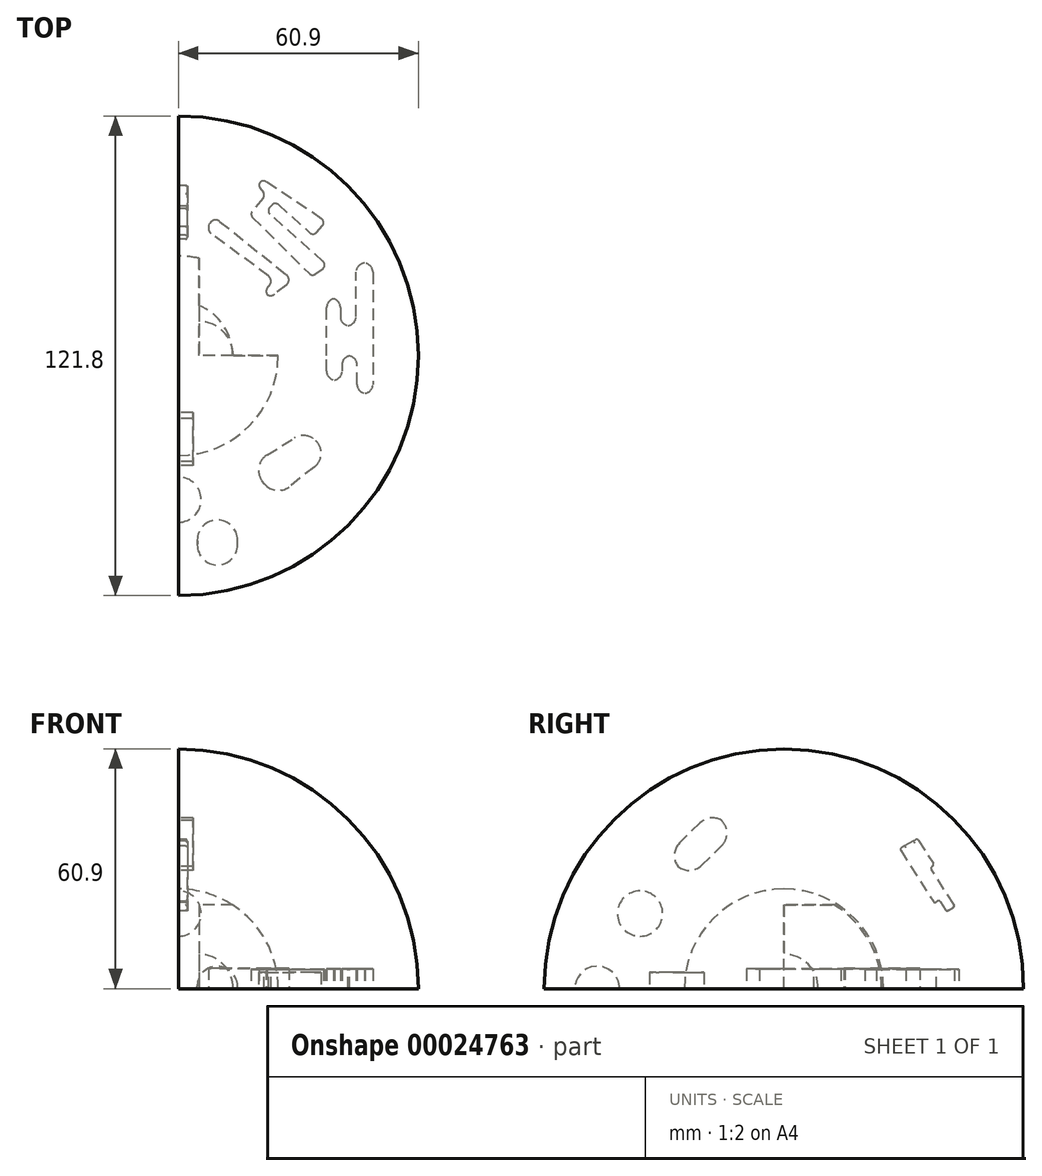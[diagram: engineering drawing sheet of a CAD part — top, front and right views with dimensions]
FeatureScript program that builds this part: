
annotation { "Feature Type Name" : "Feature", "Feature Type Description" : "" }
export const myFeature = defineFeature(function(context is Context, id is Id, definition is map)
    precondition{}
    {
        {
            var Q0;
            Q0=qCreatedBy(makeId("Front.planeOp"),FACE);
            var sketch = newSketch(context, id + "F0", { "sketchPlane" : qUnion([Q0])});
            skCircle(sketch, "E0", {"center": v(0, 0) * mm, "radius": 60.9 * mm});
            skLineSegment(sketch, "E1", {"start": v(0, 60.9) * mm, "end": v(0, -60.9) * mm});
            skSolve(sketch);
        }
        {
            var Q0;
            {var subQ0=sQuery(id+"F0.wireOp",EDGE,"E1");Q0=makeQuery(id+"F0.imprint","IMPRINT",FACE,{"disambiguationData":[TD([[makeQuery(id+"F0.imprint","IMPRINT",EDGE,{"derivedFrom":subQ0}),1.0]])]});}
            var Q1;
            Q1=sQuery(id+"F0.wireOp",EDGE,"E1");
            revolve(context, id + "F1", {"entities" : qUnion([Q0]), "axis" : qUnion([Q1]), "revolveType" : RevolveType.FULL});
        }
        {
            var Q0;
            Q0=qCreatedBy(makeId("Front.planeOp"),FACE);
            var sketch = newSketch(context, id + "F2", { "sketchPlane" : qUnion([Q0])});
            skLineSegment(sketch, "E2", {"start": v(0, 61.71) * mm, "end": v(0, 0) * mm});
            skLineSegment(sketch, "E3", {"start": v(60.99, 0) * mm, "end": v(60.99, 61.71) * mm});
            skLineSegment(sketch, "E4", {"start": v(60.99, 61.71) * mm, "end": v(0, 61.71) * mm});
            skLineSegment(sketch, "E5", {"start": v(0, 0) * mm, "end": v(60.99, 0) * mm});
            skSolve(sketch);
        }
        {
            var Q0;
            Q0=makeQuery(id+"F2.imprint","IMPRINT",FACE,{"disambiguationData":[TD([[makeQuery(id+"F2.imprint","IMPRINT",EDGE,{"derivedFrom":sQuery(id+"F2.wireOp",EDGE,"E2")}),1.0]])]});
            extrude(context, id + "F3", {"entities" : qUnion([Q0]), "operationType" : NewBodyOperationType.REMOVE, "oppositeDirection" : true, "depth" : 254 * mm});
        }
        {
            var Q0;
            Q0=makeQuery(id+"F3.boolean.opBoolean","COPY",FACE,{"derivedFrom":makeQuery(id+"F3.opExtrude","CAP_FACE",FACE,{"disambiguationData":[OSD([sQuery(id+"F2.wireOp",EDGE,"E2"),sQuery(id+"F2.wireOp",EDGE,"E3"),sQuery(id+"F2.wireOp",EDGE,"E4"),sQuery(id+"F2.wireOp",EDGE,"E5")])],"isStart":true})});
            var sketch = newSketch(context, id + "F4", { "sketchPlane" : qUnion([Q0])});
            skSolve(sketch);
        }
        {
            var Q0;
            {var subQ0=sQuery(id+"F2.wireOp",EDGE,"E2");Q0=makeQuery(id+"F4.imprint","IMPRINT",FACE,{"disambiguationData":[TD([[makeQuery(id+"F4.imprint","IMPRINT",EDGE,{"derivedFrom":makeQuery(id+"F3.boolean.opBoolean","COPY",EDGE,{"derivedFrom":makeQuery(id+"F3.opExtrude","CAP_EDGE",EDGE,{"disambiguationData":[OSD([subQ0])],"isStart":true})})}),-1.0]])]});}
            extrude(context, id + "F5", {"entities" : qUnion([Q0]), "operationType" : NewBodyOperationType.REMOVE, "oppositeDirection" : true, "depth" : 254 * mm});
        }
        {
            var Q0;
            {var subQ0=sQuery(id+"F2.wireOp",EDGE,"E2");Q0=makeQuery(id+"F5.boolean.opBoolean","MERGE",FACE,{"derivedFrom":[makeQuery(id+"F3.boolean.opBoolean","COPY",FACE,{"derivedFrom":makeQuery(id+"F3.opExtrude","SWEPT_FACE",FACE,{"disambiguationData":[OSD([subQ0])]})}),makeQuery(id+"F5.opExtrude","SWEPT_FACE",FACE,{"disambiguationData":[OSD([subQ0])]})]});}
            var sketch = newSketch(context, id + "F6", { "sketchPlane" : qUnion([Q0])});
            skLineSegment(sketch, "E6", {"start": v(-18.57, 44.8) * mm, "end": v(-29.7, 33.88) * mm});
            skLineSegment(sketch, "E7", {"start": v(-29.7, 33.88) * mm, "end": v(-24.1, 28.2) * mm});
            skLineSegment(sketch, "E8", {"start": v(-24.1, 28.2) * mm, "end": v(-12.11, 39.98) * mm});
            skLineSegment(sketch, "E9", {"start": v(-12.11, 39.98) * mm, "end": v(-18.57, 44.8) * mm});
            skSolve(sketch);
        }
        {
            var Q0;
            Q0=makeQuery(id+"F6.imprint","IMPRINT",FACE,{"disambiguationData":[TD([[makeQuery(id+"F6.imprint","IMPRINT",EDGE,{"derivedFrom":sQuery(id+"F6.wireOp",EDGE,"E6")}),1.0]])]});
            extrude(context, id + "F7", {"entities" : qUnion([Q0]), "operationType" : NewBodyOperationType.ADD, "depth" : 3.64 * mm});
        }
        {
            var Q0;
            Q0=makeQuery(id+"F7.opExtrude","SWEPT_EDGE",EDGE,{"disambiguationData":[OSD([sQuery(id+"F6.wireOp",EDGE,"E6"),sQuery(id+"F6.wireOp",EDGE,"E9")])]});
            var Q1;
            Q1=makeQuery(id+"F7.opExtrude","SWEPT_EDGE",EDGE,{"disambiguationData":[OSD([sQuery(id+"F6.wireOp",EDGE,"E8"),sQuery(id+"F6.wireOp",EDGE,"E9")])]});
            var Q2;
            Q2=makeQuery(id+"F7.opExtrude","SWEPT_EDGE",EDGE,{"disambiguationData":[OSD([sQuery(id+"F6.wireOp",EDGE,"E6"),sQuery(id+"F6.wireOp",EDGE,"E7")])]});
            var Q3;
            Q3=makeQuery(id+"F7.opExtrude","SWEPT_EDGE",EDGE,{"disambiguationData":[OSD([sQuery(id+"F6.wireOp",EDGE,"E7"),sQuery(id+"F6.wireOp",EDGE,"E8")])]});
            fillet(context, id + "F8", {"entities" : qUnion([Q0, Q1, Q2, Q3]), "radius" : 4.44 * mm, "tangentPropagation" : true, "allowEdgeOverflow" : false});
        }
        {
            var Q0;
            {var subQ0=sQuery(id+"F2.wireOp",EDGE,"E2");Q0=makeQuery(id+"F5.boolean.opBoolean","MERGE",FACE,{"derivedFrom":[makeQuery(id+"F3.boolean.opBoolean","COPY",FACE,{"derivedFrom":makeQuery(id+"F3.opExtrude","SWEPT_FACE",FACE,{"disambiguationData":[OSD([subQ0])]})}),makeQuery(id+"F5.opExtrude","SWEPT_FACE",FACE,{"disambiguationData":[OSD([subQ0])]})]});}
            var sketch = newSketch(context, id + "F9", { "sketchPlane" : qUnion([Q0])});
            skCircle(sketch, "E10", {"center": v(-36.55, 19.09) * mm, "radius": 5.75 * mm});
            skLineSegment(sketch, "E11", {"start": v(-36.55, 24.84) * mm, "end": v(-36.55, 13.34) * mm});
            skSolve(sketch);
        }
        {
            var Q0;
            {var subQ0=sQuery(id+"F9.wireOp",EDGE,"E11");Q0=makeQuery(id+"F9.imprint","IMPRINT",FACE,{"disambiguationData":[TD([[makeQuery(id+"F9.imprint","IMPRINT",EDGE,{"derivedFrom":subQ0}),1.0]])]});}
            var Q1;
            Q1=sQuery(id+"F9.wireOp",EDGE,"E11");
            revolve(context, id + "F10", {"operationType" : NewBodyOperationType.ADD, "entities" : qUnion([Q0]), "axis" : qUnion([Q1]), "revolveType" : RevolveType.FULL});
        }
        {
            var Q0;
            Q0=qCreatedBy(makeId("Front.planeOp"),FACE);
            var sketch = newSketch(context, id + "F11", { "sketchPlane" : qUnion([Q0])});
            skCircle(sketch, "E12", {"center": v(0, 0) * mm, "radius": 25.3 * mm});
            skLineSegment(sketch, "E13", {"start": v(0, 25.3) * mm, "end": v(0, -25.3) * mm});
            skSolve(sketch);
        }
        {
            var Q0;
            {var subQ0=sQuery(id+"F11.wireOp",EDGE,"E13");Q0=makeQuery(id+"F11.imprint","IMPRINT",FACE,{"disambiguationData":[TD([[makeQuery(id+"F11.imprint","IMPRINT",EDGE,{"derivedFrom":subQ0}),1.0]])]});}
            var Q1;
            Q1=sQuery(id+"F11.wireOp",EDGE,"E13");
            revolve(context, id + "F12", {"operationType" : NewBodyOperationType.ADD, "entities" : qUnion([Q0]), "axis" : qUnion([Q1]), "revolveType" : RevolveType.FULL});
        }
        {
            var Q0;
            Q0=qCreatedBy(makeId("Front.planeOp"),FACE);
            var sketch = newSketch(context, id + "F13", { "sketchPlane" : qUnion([Q0])});
            skLineSegment(sketch, "E14", {"start": v(27.47, 0) * mm, "end": v(27.47, 21.23) * mm});
            skLineSegment(sketch, "E15", {"start": v(27.47, 21.23) * mm, "end": v(5.19, 21.23) * mm});
            skLineSegment(sketch, "E16", {"start": v(5.19, 21.23) * mm, "end": v(5.19, 0) * mm});
            skLineSegment(sketch, "E17", {"start": v(5.19, 0) * mm, "end": v(27.47, 0) * mm});
            skSolve(sketch);
        }
        {
            var Q0;
            Q0=makeQuery(id+"F13.imprint","IMPRINT",FACE,{"disambiguationData":[TD([[makeQuery(id+"F13.imprint","IMPRINT",EDGE,{"derivedFrom":sQuery(id+"F13.wireOp",EDGE,"E14")}),1.0]])]});
            extrude(context, id + "F14", {"entities" : qUnion([Q0]), "operationType" : NewBodyOperationType.REMOVE, "oppositeDirection" : true, "depth" : 26.4 * mm});
        }
        {
            var Q0;
            Q0=makeQuery(id+"F14.boolean.opBoolean","COPY",FACE,{"derivedFrom":makeQuery(id+"F14.opExtrude","SWEPT_FACE",FACE,{"disambiguationData":[OSD([sQuery(id+"F13.wireOp",EDGE,"E16")])]})});
            var sketch = newSketch(context, id + "F15", { "sketchPlane" : qUnion([Q0])});
            skCircle(sketch, "E18", {"center": v(0, 0) * mm, "radius": 8.73 * mm});
            skLineSegment(sketch, "E19", {"start": v(0, 8.73) * mm, "end": v(0, -8.73) * mm});
            skSolve(sketch);
        }
        {
            var Q0;
            {var subQ0=sQuery(id+"F13.wireOp",EDGE,"E16");var subQ2=sQuery(id+"F15.wireOp",EDGE,"E18");var subQ4=sQuery(id+"F15.wireOp",EDGE,"E19");var subQ6=makeQuery(id+"F15.imprint","INTERSECT",VERTEX,{"derivedFrom":[makeQuery(id+"F14.boolean.opBoolean","COPY",EDGE,{"derivedFrom":makeQuery(id+"F14.opExtrude","CAP_EDGE",EDGE,{"disambiguationData":[OSD([subQ0])],"isStart":true})}),subQ2,subQ4]});Q0=makeQuery(id+"F15.imprint","IMPRINT",FACE,{"disambiguationData":[TD([[makeQuery(id+"F15.imprint","IMPRINT",EDGE,{"disambiguationData":[TD([[subQ6,1.0]])],"derivedFrom":subQ2}),1.0]])]});}
            var Q1;
            Q1=sQuery(id+"F15.wireOp",EDGE,"E19");
            revolve(context, id + "F16", {"operationType" : NewBodyOperationType.ADD, "entities" : qUnion([Q0]), "axis" : qUnion([Q1]), "revolveType" : RevolveType.FULL});
        }
        {
            var Q0;
            {var subQ0=sQuery(id+"F2.wireOp",EDGE,"E5");Q0=makeQuery(id+"F14.boolean.opBoolean","MERGE",FACE,{"derivedFrom":[makeQuery(id+"F5.boolean.opBoolean","MERGE",FACE,{"derivedFrom":[makeQuery(id+"F3.boolean.opBoolean","COPY",FACE,{"derivedFrom":makeQuery(id+"F3.opExtrude","SWEPT_FACE",FACE,{"disambiguationData":[OSD([subQ0])]})}),makeQuery(id+"F5.opExtrude","SWEPT_FACE",FACE,{"disambiguationData":[OSD([subQ0])]})]}),makeQuery(id+"F14.opExtrude","SWEPT_FACE",FACE,{"disambiguationData":[OSD([sQuery(id+"F13.wireOp",EDGE,"E17")])]})]});}
            var sketch = newSketch(context, id + "F17", { "sketchPlane" : qUnion([Q0])});
            skLineSegment(sketch, "E20", {"start": v(31.7, -19.5) * mm, "end": v(39.57, -24.3) * mm});
            skLineSegment(sketch, "E21", {"start": v(39.57, -24.3) * mm, "end": v(24.59, -36.02) * mm});
            skLineSegment(sketch, "E22", {"start": v(24.59, -36.02) * mm, "end": v(18.22, -27.87) * mm});
            skLineSegment(sketch, "E23", {"start": v(18.22, -27.87) * mm, "end": v(31.7, -19.5) * mm});
            skSolve(sketch);
        }
        {
            var Q0;
            Q0=makeQuery(id+"F17.imprint","IMPRINT",FACE,{"disambiguationData":[TD([[makeQuery(id+"F17.imprint","IMPRINT",EDGE,{"derivedFrom":sQuery(id+"F17.wireOp",EDGE,"E20")}),-1.0]])]});
            extrude(context, id + "F18", {"entities" : qUnion([Q0]), "operationType" : NewBodyOperationType.ADD, "depth" : 4.1 * mm});
        }
        {
            var Q0;
            Q0=makeQuery(id+"F18.opExtrude","SWEPT_EDGE",EDGE,{"disambiguationData":[OSD([sQuery(id+"F17.wireOp",EDGE,"E20"),sQuery(id+"F17.wireOp",EDGE,"E23")])]});
            var Q1;
            Q1=makeQuery(id+"F18.opExtrude","SWEPT_EDGE",EDGE,{"disambiguationData":[OSD([sQuery(id+"F17.wireOp",EDGE,"E20"),sQuery(id+"F17.wireOp",EDGE,"E21")])]});
            var Q2;
            Q2=makeQuery(id+"F18.opExtrude","SWEPT_EDGE",EDGE,{"disambiguationData":[OSD([sQuery(id+"F17.wireOp",EDGE,"E21"),sQuery(id+"F17.wireOp",EDGE,"E22")])]});
            var Q3;
            Q3=makeQuery(id+"F18.opExtrude","SWEPT_EDGE",EDGE,{"disambiguationData":[OSD([sQuery(id+"F17.wireOp",EDGE,"E22"),sQuery(id+"F17.wireOp",EDGE,"E23")])]});
            fillet(context, id + "F19", {"entities" : qUnion([Q0, Q1, Q2, Q3]), "radius" : 4.44 * mm, "tangentPropagation" : true, "allowEdgeOverflow" : false});
        }
        {
            var Q0;
            {var subQ0=sQuery(id+"F2.wireOp",EDGE,"E5");Q0=makeQuery(id+"F14.boolean.opBoolean","MERGE",FACE,{"derivedFrom":[makeQuery(id+"F5.boolean.opBoolean","MERGE",FACE,{"derivedFrom":[makeQuery(id+"F3.boolean.opBoolean","COPY",FACE,{"derivedFrom":makeQuery(id+"F3.opExtrude","SWEPT_FACE",FACE,{"disambiguationData":[OSD([subQ0])]})}),makeQuery(id+"F5.opExtrude","SWEPT_FACE",FACE,{"disambiguationData":[OSD([subQ0])]})]}),makeQuery(id+"F14.opExtrude","SWEPT_FACE",FACE,{"disambiguationData":[OSD([sQuery(id+"F13.wireOp",EDGE,"E17")])]})]});}
            var sketch = newSketch(context, id + "F20", { "sketchPlane" : qUnion([Q0])});
            skLineSegment(sketch, "E24", {"start": v(37.64, 0) * mm, "end": v(37.64, 14.54) * mm});
            skLineSegment(sketch, "E25", {"start": v(37.64, 14.54) * mm, "end": v(41.1, 14.54) * mm});
            skLineSegment(sketch, "E26", {"start": v(41.1, 14.54) * mm, "end": v(41.1, 7.66) * mm});
            skLineSegment(sketch, "E27", {"start": v(41.1, 7.66) * mm, "end": v(45.1, 7.66) * mm});
            skLineSegment(sketch, "E28", {"start": v(45.1, 7.66) * mm, "end": v(45.1, 23.52) * mm});
            skLineSegment(sketch, "E29", {"start": v(45.1, 23.52) * mm, "end": v(49.38, 23.52) * mm});
            skLineSegment(sketch, "E30", {"start": v(49.38, 23.52) * mm, "end": v(49.38, -9.53) * mm});
            skLineSegment(sketch, "E31", {"start": v(49.38, -9.53) * mm, "end": v(45.33, -9.53) * mm});
            skLineSegment(sketch, "E32", {"start": v(45.33, -9.53) * mm, "end": v(45.33, 0) * mm});
            skLineSegment(sketch, "E33", {"start": v(45.33, 0) * mm, "end": v(41.52, 0) * mm});
            skLineSegment(sketch, "E34", {"start": v(41.52, 0) * mm, "end": v(41.52, -6.22) * mm});
            skLineSegment(sketch, "E35", {"start": v(41.52, -6.22) * mm, "end": v(37.61, -6.22) * mm});
            skLineSegment(sketch, "E36", {"start": v(37.61, -6.22) * mm, "end": v(37.64, 0) * mm});
            skSolve(sketch);
        }
        {
            var Q0;
            Q0=makeQuery(id+"F20.imprint","IMPRINT",FACE,{"disambiguationData":[TD([[makeQuery(id+"F20.imprint","IMPRINT",EDGE,{"derivedFrom":sQuery(id+"F20.wireOp",EDGE,"E24")}),-1.0]])]});
            extrude(context, id + "F21", {"entities" : qUnion([Q0]), "operationType" : NewBodyOperationType.ADD, "depth" : 4.98 * mm});
        }
        {
            var Q0;
            Q0=makeQuery(id+"F21.opExtrude","SWEPT_EDGE",EDGE,{"disambiguationData":[OSD([sQuery(id+"F20.wireOp",EDGE,"E25"),sQuery(id+"F20.wireOp",EDGE,"E26")])]});
            var Q1;
            Q1=makeQuery(id+"F21.opExtrude","SWEPT_EDGE",EDGE,{"disambiguationData":[OSD([sQuery(id+"F20.wireOp",EDGE,"E28"),sQuery(id+"F20.wireOp",EDGE,"E29")])]});
            var Q2;
            Q2=makeQuery(id+"F21.opExtrude","SWEPT_EDGE",EDGE,{"disambiguationData":[OSD([sQuery(id+"F20.wireOp",EDGE,"E31"),sQuery(id+"F20.wireOp",EDGE,"E32")])]});
            var Q3;
            Q3=makeQuery(id+"F21.opExtrude","SWEPT_EDGE",EDGE,{"disambiguationData":[OSD([sQuery(id+"F20.wireOp",EDGE,"E35"),sQuery(id+"F20.wireOp",EDGE,"E36")])]});
            var Q4;
            Q4=makeQuery(id+"F21.opExtrude","SWEPT_EDGE",EDGE,{"disambiguationData":[OSD([sQuery(id+"F20.wireOp",EDGE,"E24"),sQuery(id+"F20.wireOp",EDGE,"E25")])]});
            var Q5;
            Q5=makeQuery(id+"F21.opExtrude","SWEPT_EDGE",EDGE,{"disambiguationData":[OSD([sQuery(id+"F20.wireOp",EDGE,"E34"),sQuery(id+"F20.wireOp",EDGE,"E35")])]});
            var Q6;
            Q6=makeQuery(id+"F21.opExtrude","SWEPT_EDGE",EDGE,{"disambiguationData":[OSD([sQuery(id+"F20.wireOp",EDGE,"E30"),sQuery(id+"F20.wireOp",EDGE,"E31")])]});
            var Q7;
            Q7=makeQuery(id+"F21.opExtrude","SWEPT_EDGE",EDGE,{"disambiguationData":[OSD([sQuery(id+"F20.wireOp",EDGE,"E29"),sQuery(id+"F20.wireOp",EDGE,"E30")])]});
            var Q8;
            Q8=makeQuery(id+"F21.opExtrude","SWEPT_EDGE",EDGE,{"disambiguationData":[OSD([sQuery(id+"F20.wireOp",EDGE,"E26"),sQuery(id+"F20.wireOp",EDGE,"E27")])]});
            var Q9;
            Q9=makeQuery(id+"F21.opExtrude","SWEPT_EDGE",EDGE,{"disambiguationData":[OSD([sQuery(id+"F20.wireOp",EDGE,"E27"),sQuery(id+"F20.wireOp",EDGE,"E28")])]});
            var Q10;
            Q10=makeQuery(id+"F21.opExtrude","SWEPT_EDGE",EDGE,{"disambiguationData":[OSD([sQuery(id+"F20.wireOp",EDGE,"E32"),sQuery(id+"F20.wireOp",EDGE,"E33")])]});
            var Q11;
            Q11=makeQuery(id+"F21.opExtrude","SWEPT_EDGE",EDGE,{"disambiguationData":[OSD([sQuery(id+"F20.wireOp",EDGE,"E33"),sQuery(id+"F20.wireOp",EDGE,"E34")])]});
            fillet(context, id + "F22", {"entities" : qUnion([Q0, Q1, Q2, Q3, Q4, Q5, Q6, Q7, Q8, Q9, Q10, Q11]), "radius" : 2.3 * mm, "tangentPropagation" : true, "allowEdgeOverflow" : false});
        }
        {
            var Q0;
            {var subQ0=sQuery(id+"F2.wireOp",EDGE,"E5");Q0=makeQuery(id+"F14.boolean.opBoolean","MERGE",FACE,{"derivedFrom":[makeQuery(id+"F5.boolean.opBoolean","MERGE",FACE,{"derivedFrom":[makeQuery(id+"F3.boolean.opBoolean","COPY",FACE,{"derivedFrom":makeQuery(id+"F3.opExtrude","SWEPT_FACE",FACE,{"disambiguationData":[OSD([subQ0])]})}),makeQuery(id+"F5.opExtrude","SWEPT_FACE",FACE,{"disambiguationData":[OSD([subQ0])]})]}),makeQuery(id+"F14.opExtrude","SWEPT_FACE",FACE,{"disambiguationData":[OSD([sQuery(id+"F13.wireOp",EDGE,"E17")])]})]});}
            var sketch = newSketch(context, id + "F23", { "sketchPlane" : qUnion([Q0])});
            skLineSegment(sketch, "E37", {"start": v(21.5, 16.5) * mm, "end": v(24.48, 19) * mm});
            skLineSegment(sketch, "E38", {"start": v(24.48, 19) * mm, "end": v(7.15, 31.91) * mm});
            skLineSegment(sketch, "E39", {"start": v(7.15, 31.91) * mm, "end": v(8.82, 35.43) * mm});
            skLineSegment(sketch, "E40", {"start": v(8.82, 35.43) * mm, "end": v(29.04, 19.3) * mm});
            skLineSegment(sketch, "E41", {"start": v(29.04, 19.3) * mm, "end": v(23.25, 14.74) * mm});
            skLineSegment(sketch, "E42", {"start": v(23.25, 14.74) * mm, "end": v(21.5, 16.5) * mm});
            skSolve(sketch);
        }
        {
            var Q0;
            Q0=makeQuery(id+"F23.imprint","IMPRINT",FACE,{"disambiguationData":[TD([[makeQuery(id+"F23.imprint","IMPRINT",EDGE,{"derivedFrom":sQuery(id+"F23.wireOp",EDGE,"E37")}),1.0]])]});
            var sketch = newSketch(context, id + "F24", { "sketchPlane" : qUnion([Q0])});
            skLineSegment(sketch, "E43", {"start": v(33.92, 20.18) * mm, "end": v(37.82, 22.97) * mm});
            skLineSegment(sketch, "E44", {"start": v(37.82, 22.97) * mm, "end": v(22.35, 36.76) * mm});
            skLineSegment(sketch, "E45", {"start": v(22.35, 36.76) * mm, "end": v(24.5, 39.17) * mm});
            skLineSegment(sketch, "E46", {"start": v(24.5, 39.17) * mm, "end": v(34.25, 30.47) * mm});
            skLineSegment(sketch, "E47", {"start": v(34.25, 30.47) * mm, "end": v(37.45, 34.06) * mm});
            skLineSegment(sketch, "E48", {"start": v(37.45, 34.06) * mm, "end": v(20.43, 45.42) * mm});
            skLineSegment(sketch, "E49", {"start": v(20.43, 45.42) * mm, "end": v(20.43, 43.07) * mm});
            skLineSegment(sketch, "E50", {"start": v(20.43, 43.07) * mm, "end": v(22.06, 40.72) * mm});
            skLineSegment(sketch, "E51", {"start": v(22.06, 40.72) * mm, "end": v(18.07, 35.88) * mm});
            skLineSegment(sketch, "E52", {"start": v(18.07, 35.88) * mm, "end": v(33.92, 20.18) * mm});
            skSolve(sketch);
        }
        {
            var Q0;
            Q0=makeQuery(id+"F23.imprint","IMPRINT",FACE,{"disambiguationData":[TD([[makeQuery(id+"F23.imprint","IMPRINT",EDGE,{"derivedFrom":sQuery(id+"F23.wireOp",EDGE,"E37")}),-1.0]])]});
            extrude(context, id + "F25", {"entities" : qUnion([Q0]), "operationType" : NewBodyOperationType.ADD, "depth" : 5.2 * mm});
        }
        {
            var Q0;
            Q0=makeQuery(id+"F25.opExtrude","SWEPT_EDGE",EDGE,{"disambiguationData":[OSD([sQuery(id+"F23.wireOp",EDGE,"E39"),sQuery(id+"F23.wireOp",EDGE,"E40")])]});
            var Q1;
            Q1=makeQuery(id+"F25.opExtrude","SWEPT_EDGE",EDGE,{"disambiguationData":[OSD([sQuery(id+"F23.wireOp",EDGE,"E41"),sQuery(id+"F23.wireOp",EDGE,"E42")])]});
            var Q2;
            Q2=makeQuery(id+"F25.opExtrude","SWEPT_EDGE",EDGE,{"disambiguationData":[OSD([sQuery(id+"F23.wireOp",EDGE,"E37"),sQuery(id+"F23.wireOp",EDGE,"E42")])]});
            var Q3;
            Q3=makeQuery(id+"F25.opExtrude","SWEPT_EDGE",EDGE,{"disambiguationData":[OSD([sQuery(id+"F23.wireOp",EDGE,"E40"),sQuery(id+"F23.wireOp",EDGE,"E41")])]});
            var Q4;
            Q4=makeQuery(id+"F25.opExtrude","SWEPT_EDGE",EDGE,{"disambiguationData":[OSD([sQuery(id+"F23.wireOp",EDGE,"E38"),sQuery(id+"F23.wireOp",EDGE,"E39")])]});
            var Q5;
            Q5=makeQuery(id+"F25.opExtrude","SWEPT_EDGE",EDGE,{"disambiguationData":[OSD([sQuery(id+"F23.wireOp",EDGE,"E37"),sQuery(id+"F23.wireOp",EDGE,"E38")])]});
            fillet(context, id + "F26", {"entities" : qUnion([Q0, Q1, Q2, Q3, Q4, Q5]), "radius" : 1.65 * mm, "tangentPropagation" : true, "allowEdgeOverflow" : false});
        }
        {
            var Q0;
            Q0=makeQuery(id+"F24.imprint","IMPRINT",FACE,{"disambiguationData":[TD([[makeQuery(id+"F24.imprint","IMPRINT",EDGE,{"derivedFrom":sQuery(id+"F24.wireOp",EDGE,"E43")}),1.0]])]});
            extrude(context, id + "F27", {"entities" : qUnion([Q0]), "operationType" : NewBodyOperationType.ADD, "depth" : 4.92 * mm});
        }
        {
            var Q0;
            Q0=makeQuery(id+"F27.opExtrude","SWEPT_EDGE",EDGE,{"disambiguationData":[OSD([sQuery(id+"F24.wireOp",EDGE,"E43"),sQuery(id+"F24.wireOp",EDGE,"E44")])]});
            var Q1;
            Q1=makeQuery(id+"F27.opExtrude","SWEPT_EDGE",EDGE,{"disambiguationData":[OSD([sQuery(id+"F24.wireOp",EDGE,"E44"),sQuery(id+"F24.wireOp",EDGE,"E45")])]});
            var Q2;
            Q2=makeQuery(id+"F27.opExtrude","SWEPT_EDGE",EDGE,{"disambiguationData":[OSD([sQuery(id+"F24.wireOp",EDGE,"E46"),sQuery(id+"F24.wireOp",EDGE,"E47")])]});
            var Q3;
            Q3=makeQuery(id+"F27.opExtrude","SWEPT_EDGE",EDGE,{"disambiguationData":[OSD([sQuery(id+"F24.wireOp",EDGE,"E47"),sQuery(id+"F24.wireOp",EDGE,"E48")])]});
            var Q4;
            Q4=makeQuery(id+"F27.opExtrude","SWEPT_EDGE",EDGE,{"disambiguationData":[OSD([sQuery(id+"F24.wireOp",EDGE,"E48"),sQuery(id+"F24.wireOp",EDGE,"E49")])]});
            var Q5;
            Q5=makeQuery(id+"F27.opExtrude","SWEPT_EDGE",EDGE,{"disambiguationData":[OSD([sQuery(id+"F24.wireOp",EDGE,"E49"),sQuery(id+"F24.wireOp",EDGE,"E50")])]});
            var Q6;
            Q6=makeQuery(id+"F27.opExtrude","SWEPT_EDGE",EDGE,{"disambiguationData":[OSD([sQuery(id+"F24.wireOp",EDGE,"E50"),sQuery(id+"F24.wireOp",EDGE,"E51")])]});
            var Q7;
            Q7=makeQuery(id+"F27.opExtrude","SWEPT_EDGE",EDGE,{"disambiguationData":[OSD([sQuery(id+"F24.wireOp",EDGE,"E51"),sQuery(id+"F24.wireOp",EDGE,"E52")])]});
            var Q8;
            Q8=makeQuery(id+"F27.opExtrude","SWEPT_EDGE",EDGE,{"disambiguationData":[OSD([sQuery(id+"F24.wireOp",EDGE,"E45"),sQuery(id+"F24.wireOp",EDGE,"E46")])]});
            var Q9;
            Q9=makeQuery(id+"F27.opExtrude","SWEPT_EDGE",EDGE,{"disambiguationData":[OSD([sQuery(id+"F24.wireOp",EDGE,"E43"),sQuery(id+"F24.wireOp",EDGE,"E52")])]});
            fillet(context, id + "F28", {"entities" : qUnion([Q0, Q1, Q2, Q3, Q4, Q5, Q6, Q7, Q8, Q9]), "radius" : 1.14 * mm, "tangentPropagation" : true, "allowEdgeOverflow" : false});
        }
        {
            var Q0;
            {var subQ0=sQuery(id+"F2.wireOp",EDGE,"E2");Q0=makeQuery(id+"F5.boolean.opBoolean","MERGE",FACE,{"derivedFrom":[makeQuery(id+"F3.boolean.opBoolean","COPY",FACE,{"derivedFrom":makeQuery(id+"F3.opExtrude","SWEPT_FACE",FACE,{"disambiguationData":[OSD([subQ0])]})}),makeQuery(id+"F5.opExtrude","SWEPT_FACE",FACE,{"disambiguationData":[OSD([subQ0])]})]});}
            var sketch = newSketch(context, id + "F29", { "sketchPlane" : qUnion([Q0])});
            skLineSegment(sketch, "E53", {"start": v(29.41, 35.5) * mm, "end": v(38.19, 21.73) * mm});
            skLineSegment(sketch, "E54", {"start": v(38.19, 21.73) * mm, "end": v(39.44, 22.52) * mm});
            skLineSegment(sketch, "E55", {"start": v(39.44, 22.52) * mm, "end": v(30.67, 36.29) * mm});
            skLineSegment(sketch, "E56", {"start": v(30.67, 36.29) * mm, "end": v(29.41, 35.5) * mm});
            skLineSegment(sketch, "E57", {"start": v(39.44, 22.52) * mm, "end": v(41.3, 19.59) * mm});
            skLineSegment(sketch, "E58", {"start": v(41.3, 19.59) * mm, "end": v(43.42, 20.93) * mm});
            skLineSegment(sketch, "E59", {"start": v(43.42, 20.93) * mm, "end": v(32.88, 37.5) * mm});
            skLineSegment(sketch, "E60", {"start": v(32.88, 37.5) * mm, "end": v(30.67, 36.29) * mm});
            skLineSegment(sketch, "E61", {"start": v(32.88, 37.5) * mm, "end": v(33.88, 38.13) * mm});
            skLineSegment(sketch, "E62", {"start": v(33.88, 38.13) * mm, "end": v(38.18, 31.37) * mm});
            skLineSegment(sketch, "E63", {"start": v(38.18, 31.37) * mm, "end": v(37.18, 30.73) * mm});
            skSolve(sketch);
        }
        {
            var Q0;
            Q0=makeQuery(id+"F29.imprint","IMPRINT",FACE,{"disambiguationData":[TD([[makeQuery(id+"F29.imprint","IMPRINT",EDGE,{"derivedFrom":sQuery(id+"F29.wireOp",EDGE,"E53")}),1.0]])]});
            var Q1;
            Q1=makeQuery(id+"F29.imprint","IMPRINT",FACE,{"disambiguationData":[TD([[makeQuery(id+"F29.imprint","IMPRINT",EDGE,{"derivedFrom":sQuery(id+"F29.wireOp",EDGE,"E55")}),-1.0]])]});
            var Q2;
            {var subQ1=sQuery(id+"F29.wireOp",EDGE,"E61");Q2=makeQuery(id+"F29.imprint","IMPRINT",FACE,{"disambiguationData":[TD([[makeQuery(id+"F29.imprint","IMPRINT",EDGE,{"derivedFrom":subQ1}),-1.0]])]});}
            extrude(context, id + "F30", {"entities" : qUnion([Q0, Q1, Q2]), "operationType" : NewBodyOperationType.ADD, "depth" : 2.25 * mm});
        }
        {
            var Q0;
            Q0=makeQuery(id+"F30.opExtrude","SWEPT_EDGE",EDGE,{"disambiguationData":[OSD([sQuery(id+"F29.wireOp",EDGE,"E53"),sQuery(id+"F29.wireOp",EDGE,"E56")])]});
            var Q1;
            Q1=makeQuery(id+"F30.opExtrude","SWEPT_EDGE",EDGE,{"disambiguationData":[OSD([sQuery(id+"F29.wireOp",EDGE,"E61"),sQuery(id+"F29.wireOp",EDGE,"E62")])]});
            var Q2;
            Q2=makeQuery(id+"F30.opExtrude","CAP_EDGE",EDGE,{"disambiguationData":[OSD([sQuery(id+"F29.wireOp",EDGE,"E60")])],"isStart":false});
            var Q3;
            Q3=makeQuery(id+"F30.opExtrude","SWEPT_EDGE",EDGE,{"disambiguationData":[OSD([sQuery(id+"F29.wireOp",EDGE,"E53"),sQuery(id+"F29.wireOp",EDGE,"E54")])]});
            var Q4;
            Q4=makeQuery(id+"F30.opExtrude","SWEPT_EDGE",EDGE,{"disambiguationData":[OSD([sQuery(id+"F29.wireOp",EDGE,"E57"),sQuery(id+"F29.wireOp",EDGE,"E58")])]});
            var Q5;
            Q5=makeQuery(id+"F30.opExtrude","SWEPT_EDGE",EDGE,{"disambiguationData":[OSD([sQuery(id+"F29.wireOp",EDGE,"E58"),sQuery(id+"F29.wireOp",EDGE,"E59")])]});
            var Q6;
            Q6=makeQuery(id+"F30.opExtrude","SWEPT_EDGE",EDGE,{"disambiguationData":[OSD([sQuery(id+"F29.wireOp",EDGE,"E59"),sQuery(id+"F29.wireOp",EDGE,"E63")])]});
            var Q7;
            Q7=makeQuery(id+"F30.opExtrude","SWEPT_EDGE",EDGE,{"disambiguationData":[OSD([sQuery(id+"F29.wireOp",EDGE,"E62"),sQuery(id+"F29.wireOp",EDGE,"E63")])]});
            var Q8;
            Q8=makeQuery(id+"F30.opExtrude","SWEPT_EDGE",EDGE,{"disambiguationData":[OSD([sQuery(id+"F29.wireOp",EDGE,"E54"),sQuery(id+"F29.wireOp",EDGE,"E55"),sQuery(id+"F29.wireOp",EDGE,"E57")])]});
            var Q9;
            Q9=makeQuery(id+"F30.opExtrude","CAP_EDGE",EDGE,{"disambiguationData":[OSD([sQuery(id+"F29.wireOp",EDGE,"E62")])],"isStart":false});
            var Q10;
            Q10=makeQuery(id+"F30.opExtrude","CAP_EDGE",EDGE,{"disambiguationData":[OSD([sQuery(id+"F29.wireOp",EDGE,"E62")])],"isStart":true});
            var Q11;
            Q11=makeQuery(id+"F30.opExtrude","CAP_EDGE",EDGE,{"disambiguationData":[OSD([sQuery(id+"F29.wireOp",EDGE,"E59")])],"isStart":false});
            var Q12;
            Q12=makeQuery(id+"F30.opExtrude","CAP_EDGE",EDGE,{"disambiguationData":[OSD([sQuery(id+"F29.wireOp",EDGE,"E59")])],"isStart":true});
            var Q13;
            Q13=makeQuery(id+"F30.opExtrude","CAP_EDGE",EDGE,{"disambiguationData":[OSD([sQuery(id+"F29.wireOp",EDGE,"E53")])],"isStart":false});
            var Q14;
            Q14=makeQuery(id+"F30.opExtrude","CAP_EDGE",EDGE,{"disambiguationData":[OSD([sQuery(id+"F29.wireOp",EDGE,"E53")])],"isStart":true});
            var Q15;
            Q15=makeQuery(id+"F30.opExtrude","CAP_EDGE",EDGE,{"disambiguationData":[OSD([sQuery(id+"F29.wireOp",EDGE,"E57")])],"isStart":false});
            var Q16;
            Q16=makeQuery(id+"F30.opExtrude","CAP_EDGE",EDGE,{"disambiguationData":[OSD([sQuery(id+"F29.wireOp",EDGE,"E57")])],"isStart":true});
            var Q17;
            Q17=makeQuery(id+"F30.opExtrude","CAP_EDGE",EDGE,{"disambiguationData":[OSD([sQuery(id+"F29.wireOp",EDGE,"E60")])],"isStart":true});
            var Q18;
            Q18=makeQuery(id+"F30.opExtrude","CAP_EDGE",EDGE,{"disambiguationData":[OSD([sQuery(id+"F29.wireOp",EDGE,"E54")])],"isStart":false});
            var Q19;
            Q19=makeQuery(id+"F30.opExtrude","CAP_EDGE",EDGE,{"disambiguationData":[OSD([sQuery(id+"F29.wireOp",EDGE,"E54")])],"isStart":true});
            var Q20;
            Q20=makeQuery(id+"F30.opExtrude","CAP_EDGE",EDGE,{"disambiguationData":[OSD([sQuery(id+"F29.wireOp",EDGE,"E63")])],"isStart":false});
            var Q21;
            Q21=makeQuery(id+"F30.opExtrude","CAP_EDGE",EDGE,{"disambiguationData":[OSD([sQuery(id+"F29.wireOp",EDGE,"E63")])],"isStart":true});
            var Q22;
            Q22=makeQuery(id+"F30.opExtrude","CAP_EDGE",EDGE,{"disambiguationData":[OSD([sQuery(id+"F29.wireOp",EDGE,"E56")])],"isStart":false});
            var Q23;
            Q23=makeQuery(id+"F30.opExtrude","CAP_EDGE",EDGE,{"disambiguationData":[OSD([sQuery(id+"F29.wireOp",EDGE,"E61")])],"isStart":false});
            var Q24;
            Q24=makeQuery(id+"F30.opExtrude","CAP_EDGE",EDGE,{"disambiguationData":[OSD([sQuery(id+"F29.wireOp",EDGE,"E56")])],"isStart":true});
            var Q25;
            Q25=makeQuery(id+"F30.opExtrude","CAP_EDGE",EDGE,{"disambiguationData":[OSD([sQuery(id+"F29.wireOp",EDGE,"E61")])],"isStart":true});
            fillet(context, id + "F31", {"entities" : qUnion([Q0, Q1, Q2, Q3, Q4, Q5, Q6, Q7, Q8, Q9, Q10, Q11, Q12, Q13, Q14, Q15, Q16, Q17, Q18, Q19, Q20, Q21, Q22, Q23, Q24, Q25]), "radius" : 0.5 * mm, "tangentPropagation" : true, "allowEdgeOverflow" : false});
        }
        {
            var Q0;
            {var subQ0=sQuery(id+"F2.wireOp",EDGE,"E5");Q0=makeQuery(id+"F14.boolean.opBoolean","MERGE",FACE,{"derivedFrom":[makeQuery(id+"F5.boolean.opBoolean","MERGE",FACE,{"derivedFrom":[makeQuery(id+"F3.boolean.opBoolean","COPY",FACE,{"derivedFrom":makeQuery(id+"F3.opExtrude","SWEPT_FACE",FACE,{"disambiguationData":[OSD([subQ0])]})}),makeQuery(id+"F5.opExtrude","SWEPT_FACE",FACE,{"disambiguationData":[OSD([subQ0])]})]}),makeQuery(id+"F14.opExtrude","SWEPT_FACE",FACE,{"disambiguationData":[OSD([sQuery(id+"F13.wireOp",EDGE,"E17")])]})]});}
            var sketch = newSketch(context, id + "F32", { "sketchPlane" : qUnion([Q0])});
            skCircle(sketch, "E64", {"center": v(9.87, -46.82) * mm, "radius": 5.1 * mm});
            skLineSegment(sketch, "E65", {"start": v(4.8, -47.43) * mm, "end": v(14.94, -47.43) * mm});
            skSolve(sketch);
        }
        {
            var Q0;
            {var subQ0=sQuery(id+"F32.wireOp",EDGE,"E65");Q0=makeQuery(id+"F32.imprint","IMPRINT",FACE,{"disambiguationData":[TD([[makeQuery(id+"F32.imprint","IMPRINT",EDGE,{"derivedFrom":subQ0}),1.0]])]});}
            var Q1;
            Q1=sQuery(id+"F32.wireOp",EDGE,"E65");
            revolve(context, id + "F33", {"operationType" : NewBodyOperationType.ADD, "entities" : qUnion([Q0]), "axis" : qUnion([Q1]), "revolveType" : RevolveType.FULL});
        }
    });
